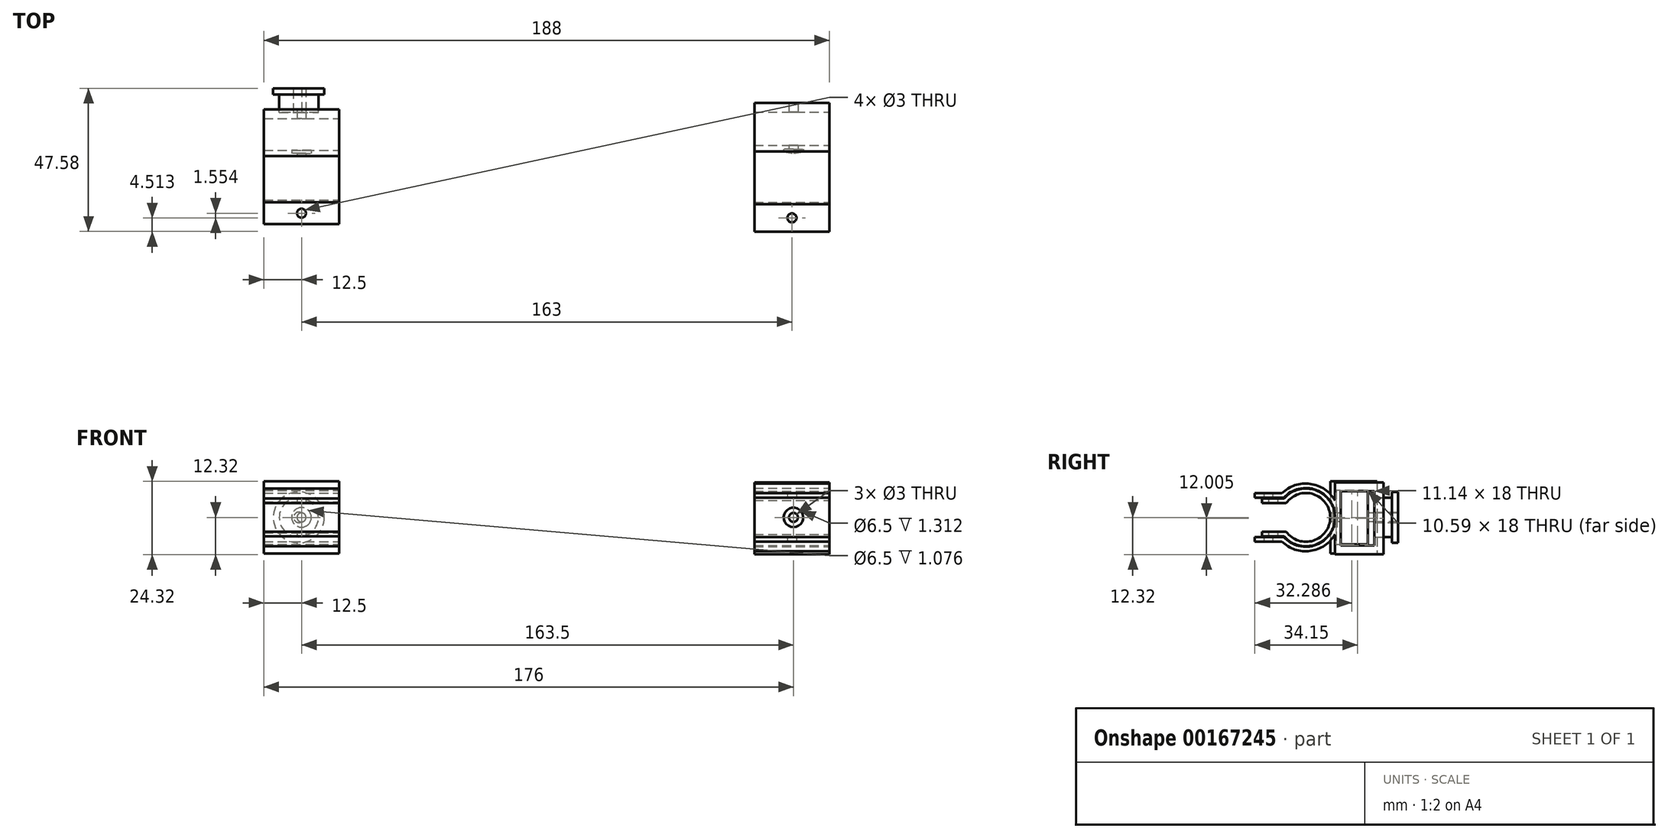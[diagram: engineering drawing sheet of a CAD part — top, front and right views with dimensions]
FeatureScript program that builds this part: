
annotation { "Feature Type Name" : "Feature", "Feature Type Description" : "" }
export const myFeature = defineFeature(function(context is Context, id is Id, definition is map)
    precondition{}
    {
        {
            var Q0;
            Q0=qCreatedBy(makeId("Front.planeOp"),FACE);
            var sketch = newSketch(context, id + "F0", { "sketchPlane" : qUnion([Q0])});
            skCircle(sketch, "E0", {"center": v(-164.4, 0) * mm, "radius": 6.5 * mm});
            skCircle(sketch, "E1", {"center": v(-164.4, 0) * mm, "radius": 8.5 * mm});
            skCircle(sketch, "E2", {"center": v(-164.4, 0) * mm, "radius": 1.75 * mm});
            skSolve(sketch);
        }
        {
            var Q0;
            Q0=qSketchRegion(id+"F0",true);
            var Q1;
            Q1=makeQuery(id+"F0.imprint","IMPRINT",FACE,{"disambiguationData":[TD([[makeQuery(id+"F0.imprint","IMPRINT",EDGE,{"derivedFrom":makeQuery(id+"FfgFavTl2RamtKQ_1.extrude1.opExtrude","CAP_EDGE",EDGE,{"disambiguationData":[OSD([sQuery(id+"FfgFavTl2RamtKQ_1.gearSketch.wireOp",EDGE,"Center")])],"isStart":false})}),-1.0]])]});
            extrude(context, id + "F1", {"entities" : qUnion([Q0, Q1]), "depth" : 2 * mm});
        }
        {
            var Q0;
            Q0=makeQuery(id+"F0.imprint","IMPRINT",FACE,{"disambiguationData":[TD([[makeQuery(id+"F0.imprint","IMPRINT",EDGE,{"derivedFrom":makeQuery(id+"FfgFavTl2RamtKQ_1.extrude1.opExtrude","CAP_EDGE",EDGE,{"disambiguationData":[OSD([sQuery(id+"FfgFavTl2RamtKQ_1.gearSketch.wireOp",EDGE,"Center")])],"isStart":false})}),-1.0]])]});
            var Q1;
            Q1=makeQuery(id+"F0.imprint","IMPRINT",FACE,{"disambiguationData":[TD([[makeQuery(id+"F0.imprint","IMPRINT",EDGE,{"derivedFrom":sQuery(id+"F0.wireOp",EDGE,"E0")}),1.0]])]});
            extrude(context, id + "F2", {"entities" : qUnion([Q0, Q1]), "operationType" : NewBodyOperationType.ADD, "depth" : (6 + 2) * mm});
        }
        {
            var Q0;
            Q0=qCreatedBy(makeId("Right.planeOp"),FACE);
            cPlane(context, id + "F3", {"entities" : qUnion([Q0]), "cplaneType" : CPlaneType.OFFSET, "offset" : 12 * mm, "width" : 150 * mm, "height" : 150 * mm});
        }
        {
            var Q0;
            Q0=qCreatedBy(id+"F3.planeOp",FACE);
            var sketch = newSketch(context, id + "F4", { "sketchPlane" : qUnion([Q0])});
            skArc(sketch, "E3", {"start": v(-37.91, -6.52) * mm, "mid": v(-20.91, 0) * mm, "end": v(-37.91, 6.52) * mm});
            skArc(sketch, "E4", {"start": v(-39.83, -6.52) * mm, "mid": v(-19.41, 0) * mm, "end": v(-39.83, 6.52) * mm});
            skLineSegment(sketch, "E5", {"start": v(-36.2, -8.02) * mm, "end": v(-47.58, -8.02) * mm});
            skLineSegment(sketch, "E6", {"start": v(-47.58, -8.02) * mm, "end": v(-47.58, -6.52) * mm});
            skLineSegment(sketch, "E7", {"start": v(-47.58, -6.52) * mm, "end": v(-37.91, -6.52) * mm});
            skLineSegment(sketch, "E8", {"start": v(-30.66, 0) * mm, "end": v(-50.27, 0) * mm, "construction": true});
            skLineSegment(sketch, "E9.MirrorCS", {"start": v(-47.58, 6.52) * mm, "end": v(-37.91, 6.52) * mm});
            skLineSegment(sketch, "E10.MirrorCS", {"start": v(-47.58, 8.02) * mm, "end": v(-47.58, 6.52) * mm});
            skLineSegment(sketch, "E11.MirrorCS", {"start": v(-36.2, 8.02) * mm, "end": v(-47.58, 8.02) * mm});
            skLineSegment(sketch, "E12", {"start": v(-20.91, -12.32) * mm, "end": v(-20.91, 11.68) * mm});
            skLineSegment(sketch, "E13", {"start": v(-20.91, -12.32) * mm, "end": v(-4.86, -12.32) * mm});
            skLineSegment(sketch, "E14", {"start": v(-4.86, -12.32) * mm, "end": v(-4.86, 11.68) * mm});
            skLineSegment(sketch, "E15", {"start": v(-20.91, 11.68) * mm, "end": v(-4.86, 11.68) * mm});
            skLineSegment(sketch, "E16", {"start": v(-19, -9.32) * mm, "end": v(-7.86, -9.32) * mm});
            skLineSegment(sketch, "E17", {"start": v(-7.86, -9.32) * mm, "end": v(-7.86, 8.68) * mm});
            skLineSegment(sketch, "E18", {"start": v(-7.86, 8.68) * mm, "end": v(-19, 8.68) * mm});
            skLineSegment(sketch, "E19", {"start": v(-19, 8.68) * mm, "end": v(-19, -9.32) * mm});
            skSolve(sketch);
        }
        {
            var Q0;
            Q0=qSketchRegion(id+"F4",true);
            extrude(context, id + "F5", {"entities" : qUnion([Q0]), "oppositeDirection" : true, "depth" : 25 * mm});
        }
        {
            var Q0;
            Q0=qCreatedBy(makeId("Right.planeOp"),FACE);
            cPlane(context, id + "F6", {"entities" : qUnion([Q0]), "cplaneType" : CPlaneType.OFFSET, "offset" : 151 * mm, "oppositeDirection" : true, "width" : 150 * mm, "height" : 150 * mm});
        }
        {
            var Q0;
            Q0=qCreatedBy(id+"F6.planeOp",FACE);
            var sketch = newSketch(context, id + "F7", { "sketchPlane" : qUnion([Q0])});
            skLineSegment(sketch, "E20.0.4", {"start": v(-7, 12) * mm, "end": v(-22.5, 12) * mm});
            skLineSegment(sketch, "E20.0.8", {"start": v(-22.5, -12) * mm, "end": v(-7, -12) * mm});
            skLineSegment(sketch, "E21", {"start": v(-22.5, 12) * mm, "end": v(-22.5, -12) * mm});
            skLineSegment(sketch, "E22.0.0", {"start": v(-20.59, -9) * mm, "end": v(-10, -9) * mm});
            skLineSegment(sketch, "E22.0.1", {"start": v(-10, -9) * mm, "end": v(-10, 9) * mm});
            skLineSegment(sketch, "E22.0.2", {"start": v(-10, 9) * mm, "end": v(-20.59, 9) * mm});
            skLineSegment(sketch, "E22.0.3", {"start": v(-20.59, 9) * mm, "end": v(-20.59, -9) * mm});
            skArc(sketch, "E23", {"start": v(-37.14, -4.78) * mm, "mid": v(-22.5, 0) * mm, "end": v(-37.14, 4.78) * mm});
            skArc(sketch, "E24", {"start": v(-38.92, -4.78) * mm, "mid": v(-21, 0) * mm, "end": v(-38.92, 4.78) * mm});
            skLineSegment(sketch, "E25", {"start": v(-37.86, 6.28) * mm, "end": v(-45.17, 6.28) * mm});
            skLineSegment(sketch, "E26", {"start": v(-45.17, 6.28) * mm, "end": v(-45.17, 4.78) * mm});
            skLineSegment(sketch, "E27", {"start": v(-45.17, 4.78) * mm, "end": v(-37.14, 4.78) * mm});
            skLineSegment(sketch, "E28.MirrorCS", {"start": v(-45.17, -4.78) * mm, "end": v(-37.14, -4.78) * mm});
            skLineSegment(sketch, "E29.MirrorCS", {"start": v(-37.86, -6.28) * mm, "end": v(-45.17, -6.28) * mm});
            skLineSegment(sketch, "E30.MirrorCS", {"start": v(-45.17, -6.28) * mm, "end": v(-45.17, -4.78) * mm});
            skLineSegment(sketch, "E31", {"start": v(-7, 12) * mm, "end": v(-7, -12) * mm});
            skSolve(sketch);
        }
        {
            var Q0;
            Q0=qSketchRegion(id+"F7",true);
            extrude(context, id + "F8", {"entities" : qUnion([Q0]), "oppositeDirection" : true, "depth" : 25 * mm});
        }
        {
            var Q0;
            Q0=makeQuery(id+"F5.opExtrude","CAP_EDGE",EDGE,{"disambiguationData":[OSD([sQuery(id+"F4.wireOp",EDGE,"E3")])],"isStart":true});
            cPoint(context, id + "F9", {"entities" : qUnion([Q0]), "parameter" : 0.5});
        }
        {
            var Q0;
            Q0=qCreatedBy(id+"F9",VERTEX);
            var Q1;
            Q1=makeQuery(id+"F5.opExtrude","CAP_EDGE",EDGE,{"disambiguationData":[OSD([sQuery(id+"F4.wireOp",EDGE,"E9.MirrorCS")])],"isStart":true});
            cPlane(context, id + "F10", {"entities" : qUnion([Q0, Q1]), "cplaneType" : CPlaneType.LINE_POINT, "offset" : 25 * mm, "width" : 150 * mm, "height" : 150 * mm});
        }
        {
            var Q0;
            Q0=qCreatedBy(id+"F10.planeOp",FACE);
            var sketch = newSketch(context, id + "F11", { "sketchPlane" : qUnion([Q0])});
            skPoint(sketch, "E32.0", {"position": v(0, 0) * mm});
            skCircle(sketch, "E33", {"center": v(0, 0) * mm, "radius": 3.25 * mm});
            skCircle(sketch, "E34", {"center": v(0, 0) * mm, "radius": 1.5 * mm});
            skCircle(sketch, "E35", {"center": v(163.5, 0) * mm, "radius": 1.5 * mm});
            skCircle(sketch, "E36", {"center": v(163.5, 0) * mm, "radius": 3.25 * mm});
            skSolve(sketch);
        }
        {
            var Q0;
            Q0=qSketchRegion(id+"F11",true);
            extrude(context, id + "F12", {"entities" : qUnion([Q0]), "operationType" : NewBodyOperationType.REMOVE, "endBound" : BoundingType.SYMMETRIC, "depth" : 1.5 * mm});
        }
        {
            var Q0;
            Q0=makeQuery(id+"F11.imprint","IMPRINT",FACE,{"disambiguationData":[TD([[makeQuery(id+"F11.imprint","IMPRINT",EDGE,{"derivedFrom":sQuery(id+"F11.wireOp",EDGE,"E35")}),1.0]])]});
            var Q1;
            Q1=makeQuery(id+"F11.imprint","IMPRINT",FACE,{"disambiguationData":[TD([[makeQuery(id+"F11.imprint","IMPRINT",EDGE,{"derivedFrom":sQuery(id+"F11.wireOp",EDGE,"55d919cf-7183-4502-b2ab-8ad903304758.0")}),-1.0]])]});
            var Q2;
            Q2=makeQuery(id+"F11.imprint","IMPRINT",FACE,{"disambiguationData":[TD([[makeQuery(id+"F11.imprint","IMPRINT",EDGE,{"derivedFrom":sQuery(id+"F11.wireOp",EDGE,"E34")}),1.0]])]});
            extrude(context, id + "F13", {"entities" : qUnion([Q0, Q1, Q2]), "operationType" : NewBodyOperationType.REMOVE, "depth" : 30.5 * mm, "hasSecondDirection" : true, "secondDirectionOppositeDirection" : true, "secondDirectionDepth" : 1.4 * mm});
        }
        {
            var Q0;
            Q0=makeQuery(id+"F5.opExtrude","SWEPT_FACE",FACE,{"disambiguationData":[OSD([sQuery(id+"F4.wireOp",EDGE,"E5")])]});
            var sketch = newSketch(context, id + "F14", { "sketchPlane" : qUnion([Q0])});
            skCircle(sketch, "E37", {"center": v(-0.5, 43.07) * mm, "radius": 1.5 * mm});
            skPoint(sketch, "E37.centerSnap0", {"position": v(-0.5, 47.58) * mm});
            skPoint(sketch, "E37.centerSnap1", {"position": v(-13, 43.07) * mm});
            skCircle(sketch, "E38", {"center": v(-163.5, 41.51) * mm, "radius": 1.5 * mm});
            skSolve(sketch);
        }
        {
            var Q0;
            Q0=qSketchRegion(id+"F14",true);
            extrude(context, id + "F15", {"entities" : qUnion([Q0]), "operationType" : NewBodyOperationType.REMOVE, "oppositeDirection" : true, "depth" : 25 * mm});
        }
    });
